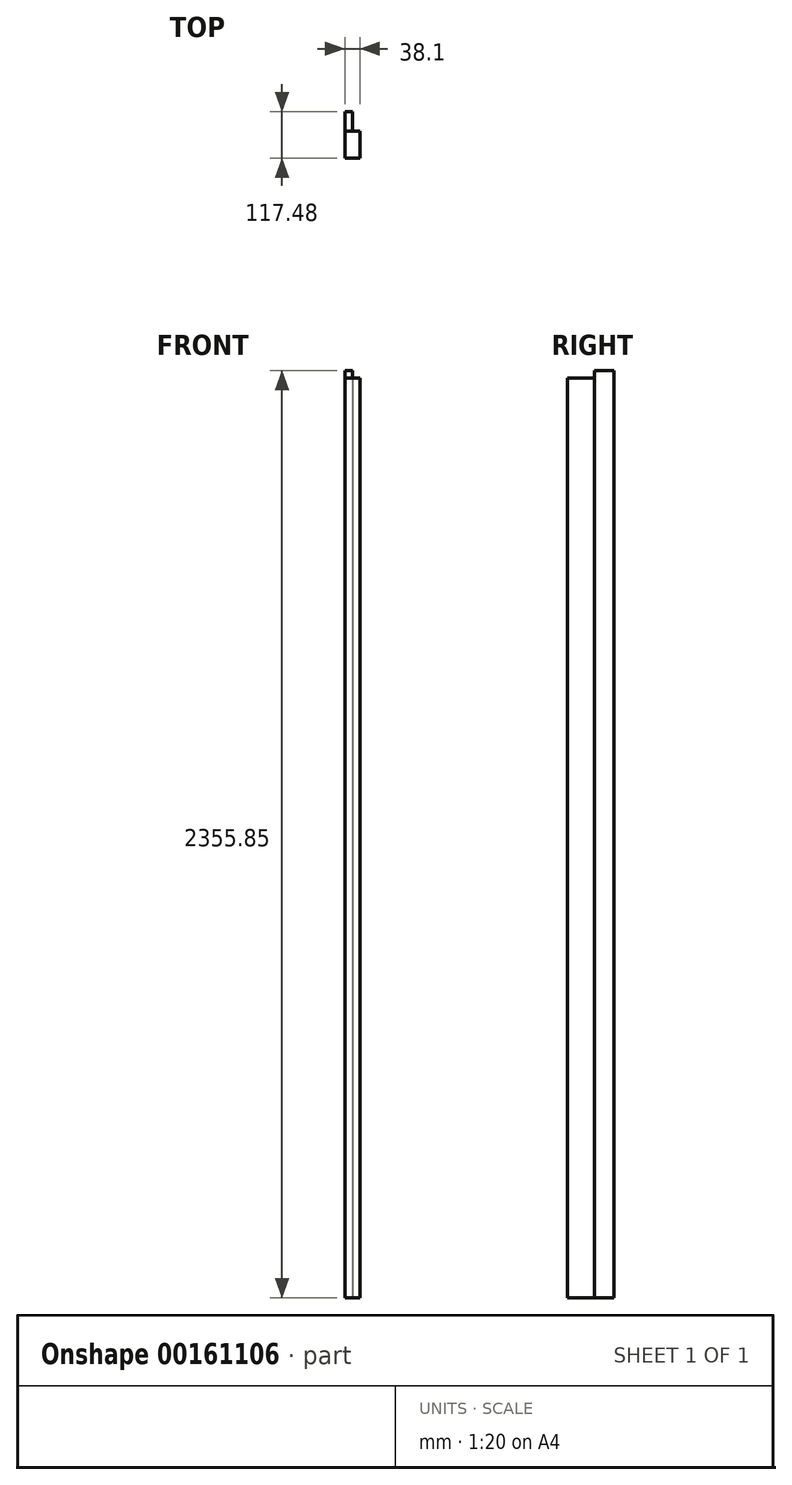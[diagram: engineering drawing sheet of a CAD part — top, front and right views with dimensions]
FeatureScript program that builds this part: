
annotation { "Feature Type Name" : "Feature", "Feature Type Description" : "" }
export const myFeature = defineFeature(function(context is Context, id is Id, definition is map)
    precondition{}
    {
        {
            var Q0;
            Q0=qCreatedBy(makeId("Top.planeOp"),FACE);
            var sketch = newSketch(context, id + "F0", { "sketchPlane" : qUnion([Q0])});
            skLineSegment(sketch, "E0", {"start": v(-2.14, 36.7) * mm, "end": v(-21.19, 36.7) * mm});
            skLineSegment(sketch, "E1", {"start": v(16.91, -80.78) * mm, "end": v(16.91, -12.52) * mm});
            skLineSegment(sketch, "E2", {"start": v(16.91, -12.52) * mm, "end": v(-2.14, -12.52) * mm});
            skLineSegment(sketch, "E3", {"start": v(-2.14, -12.52) * mm, "end": v(-2.14, 36.7) * mm});
            skLineSegment(sketch, "E4", {"start": v(-21.19, 36.7) * mm, "end": v(-21.19, -80.78) * mm});
            skLineSegment(sketch, "E5", {"start": v(-21.19, -80.78) * mm, "end": v(16.91, -80.78) * mm});
            skSolve(sketch);
        }
        {
            var Q0;
            Q0=qSketchRegion(id+"F0",true);
            extrude(context, id + "F1", {"entities" : qUnion([Q0]), "depth" : 2355.85 * mm});
        }
        {
            var Q0;
            Q0=qCreatedBy(makeId("Right.planeOp"),FACE);
            var sketch = newSketch(context, id + "F2", { "sketchPlane" : qUnion([Q0])});
            skLineSegment(sketch, "E6.0", {"start": v(-80.78, 2355.85) * mm, "end": v(-12.52, 2355.85) * mm});
            skLineSegment(sketch, "E7", {"start": v(-80.78, 2355.85) * mm, "end": v(-80.78, 2336.8) * mm});
            skLineSegment(sketch, "E8", {"start": v(-80.78, 2336.8) * mm, "end": v(-12.52, 2336.8) * mm});
            skLineSegment(sketch, "E9", {"start": v(-12.52, 2336.8) * mm, "end": v(-12.52, 2355.85) * mm});
            skSolve(sketch);
        }
        {
            var Q0;
            Q0 = qSketchRegion(id + "F2", true);
            extrude(context, id + "F3", {"entities" : qUnion([Q0]), "operationType" : NewBodyOperationType.REMOVE, "endBound" : BoundingType.THROUGH_ALL, "oppositeDirection" : true, "depth" : 25.4 * mm, "hasSecondDirection" : true, "secondDirectionBound" : SecondDirectionBoundingType.THROUGH_ALL, "secondDirectionOppositeDirection" : false, "secondDirectionDepth" : 25.4 * mm});
        }
    });
